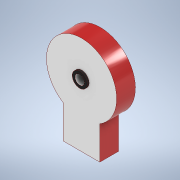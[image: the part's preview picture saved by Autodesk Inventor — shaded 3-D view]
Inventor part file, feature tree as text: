
AUTODESK INVENTOR PART (.ipt)
format: ipt  version: 2022 (Build 260153000, 153)  size: 133,632 bytes
history: native  units: mm
features: extrude x4, sketch x4
ambient origin geometry x8: Origin, YZ Plane, XZ Plane, XY Plane, X Axis, Y Axis, Z Axis, Center Point
bodies: Solid1 (feature_tree)
feature tree (8):
  extrude  "Extrusion1"  TaperAngle=0.0deg  [1 undecoded]
  extrude  "Extrusion2"  Depth=8.0mm TaperAngle=0.0deg
  sketch  "Sketch3"
  sketch  "Sketch4"
  extrude  "Extrusion3"  [1 undecoded]
  extrude  "Extrusion4"  [1 undecoded]
  sketch  "Sketch1"  dims[d0=80.0mm d1=0.0mm d2=0.0mm d3=0.0mm]
  sketch  "Sketch2"  dims[d4=8.0mm d5=0.0mm d6=8.0mm d7=0.0mm]
note: 3 required parameter values undecoded (feature->parameter linkage not recoverable at this tier; creation-order binding heuristic only, values carry confidence <= 0.55)
